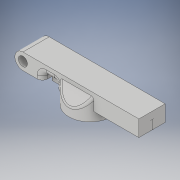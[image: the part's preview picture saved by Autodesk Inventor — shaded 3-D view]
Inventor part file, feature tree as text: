
AUTODESK INVENTOR PART (.ipt)
format: ipt  version: 2019 (Build 230136000, 136)  size: 348,672 bytes
history: native  units: in
note: dims shown in document units (in); Inventor stores cm internally (conversion verified against a paired STEP export)
features: extrude x7, sketch x7, fillet x6, chamfer x2
ambient origin geometry x8: Origin, YZ Plane, XZ Plane, XY Plane, X Axis, Y Axis, Z Axis, Center Point
bodies: Solid1 (feature_tree)
feature tree (22):
  extrude  "Extrusion1"  Depth=2.5709in
  extrude  "Extrusion2"  Depth=0.5827in TaperAngle=0.0deg
  extrude  "Extrusion3"  Depth=0.1969in TaperAngle=0.0deg
  chamfer  "Chamfer3"  Distance=0.1969in
  chamfer  "Chamfer4"  Distance=1.378in
  fillet  "Fillet4"  Radius=0.5827in
  fillet  "Fillet5"  Radius=0.2756in
  extrude  "Extrusion6"  Depth=0.1811in TaperAngle=120.0deg
  extrude  "Extrusion7"  Depth=0.0787in
  extrude  "Extrusion8"  Depth=0.0787in
  extrude  "Extrusion9"  Depth=0.8661in
  fillet  "Fillet6"  Radius=0.0394in
  fillet  "Fillet7"  Radius=0.5827in
  fillet  "Fillet8"  Radius=0.2913in
  fillet  "Fillet9"  Radius=0.0787in
  sketch  "Sketch1"  dims[d0=0.2008in d2=2.5709in]
  sketch  "Sketch2"  dims[d3=0.1791in d4=0.5827in d5=0.0in]
  sketch  "Sketch3"  dims[d6=0.5118in d7=0.1969in d8=0.0in]
  sketch  "Sketch10"  dims[d9=2.315in]
  sketch  "Sketch11"  dims[d11=0.9449in d13=0.1969in d14=0.0in]
  sketch  "Sketch12"  dims[d15=0.2913in]
  sketch  "Sketch13"  dims[d16=0.2913in d30=1.378in d45=0.5827in d46=0.2756in d47=0.1811in d48=120.0deg d49=0.1811in d50=0.2756in d51=120.0deg d52=0.0787in d53=0.0787in d54=0.8661in d55=0.0394in d56=0.0in d57=0.5827in d58=0.2913in d63=0.0787in d64=0.0394in d65=0.5827in d66=0.0in d67=0.1575in d68=0.5827in d69=0.2126in d70=0.2362in d71=0.0in d72=0.0787in d73=0.1575in d74=0.0787in d75=0.0787in d76=0.1575in d77=0.0in d78=0.1181in d79=0.0394in d80=0.0394in d81=0.0394in]
